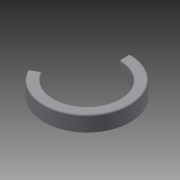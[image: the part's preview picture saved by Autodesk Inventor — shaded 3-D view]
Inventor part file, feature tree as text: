
AUTODESK INVENTOR PART (.ipt)
format: ipt  version: 2015 (Build 190159000, 159)  size: 124,416 bytes
history: native  units: in
note: dims shown in document units (in); Inventor stores cm internally (conversion verified against a paired STEP export)
features: fillet x2, revolve x1, sketch x1
ambient origin geometry x8: Origin, YZ Plane, XZ Plane, XY Plane, X Axis, Y Axis, Z Axis, Center Point
bodies: Solid1 (feature_tree)
feature tree (4):
  revolve  "Revolution1"  [1 undecoded]
  fillet  "Fillet1"  Radius=2.5in
  fillet  "Fillet2"  Radius=0.0625in
  sketch  "Sketch1"  dims[d0=2.2in d1=1.75in d2=2.5in d3=0.0625in d4=90.0deg d5=0.125in d6=0.0625in d7=2.5in d8=1.5in d9=90.0deg d10=5.5in d11=240.0deg d12=0.25in d13=0.25in]
note: 1 required parameter value undecoded (feature->parameter linkage not recoverable at this tier; creation-order binding heuristic only, values carry confidence <= 0.55)
